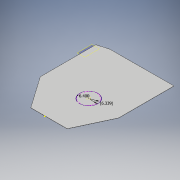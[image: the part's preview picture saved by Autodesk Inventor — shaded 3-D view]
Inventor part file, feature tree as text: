
AUTODESK INVENTOR PART (.ipt)
format: ipt  version: 2018 (Build 220112000, 112)  size: 131,584 bytes
history: native  units: in
note: dims shown in document units (in); Inventor stores cm internally (conversion verified against a paired STEP export)
features: other x9, reference x7, sketch x4, extrude x3, plane x1
ambient origin geometry x8: Origin, YZ Plane, XZ Plane, XY Plane, X Axis, Y Axis, Z Axis, Center Point
bodies: Solid1 (feature_tree)
feature tree (24):
  other  "Table"
  other  "side cover plate-01"
  other  "side cover plate-02"
  plane  "Work Plane1"
  extrude  "Plate extrude"  Depth=0.063in
  extrude  "Tailstock door"  Depth=0.063in TaperAngle=0.0deg
  extrude  "Headstock cut out"  Depth=6.3386in
  sketch  "Sketch5"  dims[d9=0.063in d10=0.0in]
  reference  "Reference2"
  reference  "Reference5"
  reference  "Reference6"
  sketch  "Sketch2"  dims[d0=0.063in d1=0.0in d3=11.811in]
  sketch  "Sketch3"  dims[d4=11.811in d5=0.063in d6=0.0in]
  reference  "Reference7"
  reference  "Reference8"
  sketch  "Sketch4"  dims[d7=6.4in d8=6.3386in]
  reference  "Reference9"
  reference  "Reference10"
  other  "Lathe Model 2018.iam"
  other  "front:1"
  other  "back plate:1"
  other  "Gearbox:1"
  other  "connecting wheel:1"
  other  "polycarbonate cover:1"
